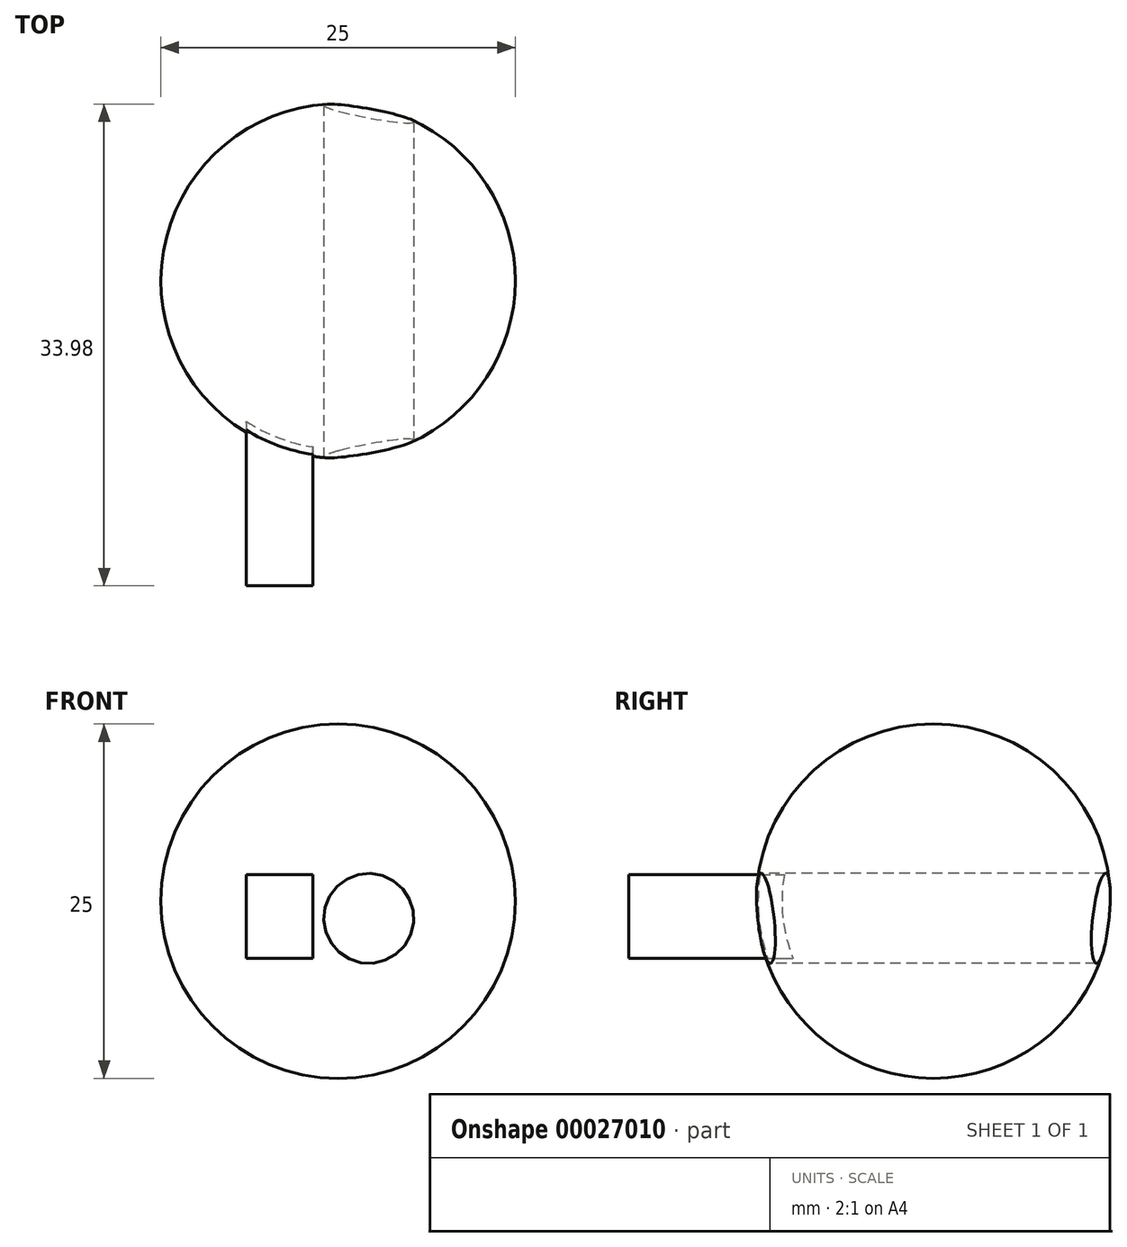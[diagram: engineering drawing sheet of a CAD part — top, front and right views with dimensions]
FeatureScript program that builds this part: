
annotation { "Feature Type Name" : "Feature", "Feature Type Description" : "" }
export const myFeature = defineFeature(function(context is Context, id is Id, definition is map)
    precondition{}
    {
        {
            var Q0;
            Q0=qCreatedBy(makeId("Front.planeOp"),FACE);
            var sketch = newSketch(context, id + "F0", { "sketchPlane" : qUnion([Q0])});
            skArc(sketch, "E0", {"start": v(-23.27, 31.46) * mm, "mid": v(-35.77, 18.96) * mm, "end": v(-23.27, 6.46) * mm});
            skLineSegment(sketch, "E1", {"start": v(-23.27, 31.46) * mm, "end": v(-23.27, 6.46) * mm});
            skSolve(sketch);
        }
        {
            var Q0;
            Q0=makeQuery(id+"F0.imprint","IMPRINT",FACE,{"disambiguationData":[TD([[makeQuery(id+"F0.imprint","IMPRINT",EDGE,{"derivedFrom":sQuery(id+"F0.wireOp",EDGE,"E0")}),1.0]])]});
            var Q1;
            Q1=sQuery(id+"F0.wireOp",EDGE,"E1");
            revolve(context, id + "F1", {"entities" : qUnion([Q0]), "axis" : qUnion([Q1]), "revolveType" : RevolveType.FULL});
        }
        {
            var Q0;
            Q0=qCreatedBy(makeId("Front.planeOp"),FACE);
            cPlane(context, id + "F2", {"entities" : qUnion([Q0]), "cplaneType" : CPlaneType.OFFSET, "offset" : 12.5 * mm, "width" : 152.4 * mm, "height" : 152.4 * mm});
        }
        {
            var Q0;
            Q0=qCreatedBy(id+"F2.planeOp",FACE);
            var sketch = newSketch(context, id + "F3", { "sketchPlane" : qUnion([Q0])});
            skCircle(sketch, "E2", {"center": v(-21.1, 17.75) * mm, "radius": 5 * mm});
            skSolve(sketch);
        }
        {
            var Q0;
            Q0=sQuery(id+"F3.wireOp",VERTEX,"E2.center");
            var Q1;
            Q1=makeQuery(id+"F1.opRevolve","SWEPT_BODY",BODY,{"disambiguationData":[OSD([sQuery(id+"F0.wireOp",EDGE,"E0"),sQuery(id+"F0.wireOp",EDGE,"E1")])]});
            hole(context, id + "F4", {"style" : HoleStyle.SIMPLE, "holeDiameter" : 6.35 * mm, "endStyle" : HoleEndStyle.THROUGH, "locations" : qUnion([Q0]), "scope" : qUnion([Q1])});
        }
        {
            var Q0;
            Q0=qCreatedBy(id+"F2.planeOp",FACE);
            var sketch = newSketch(context, id + "F5", { "sketchPlane" : qUnion([Q0])});
            skLineSegment(sketch, "E3.bottom", {"start": v(-25.06, 14.94) * mm, "end": v(-29.76, 14.94) * mm});
            skLineSegment(sketch, "E3.top", {"start": v(-25.06, 20.83) * mm, "end": v(-29.76, 20.83) * mm});
            skLineSegment(sketch, "E3.left", {"start": v(-25.06, 14.94) * mm, "end": v(-25.06, 20.83) * mm});
            skLineSegment(sketch, "E3.right", {"start": v(-29.76, 14.94) * mm, "end": v(-29.76, 20.83) * mm});
            skSolve(sketch);
        }
        {
            var Q0;
            Q0=makeQuery(id+"F5.imprint","IMPRINT",FACE,{"disambiguationData":[TD([[makeQuery(id+"F5.imprint","IMPRINT",EDGE,{"derivedFrom":sQuery(id+"F5.wireOp",EDGE,"E3.bottom")}),-1.0]])]});
            extrude(context, id + "F6", {"entities" : qUnion([Q0]), "operationType" : NewBodyOperationType.ADD, "depth" : 9 * mm, "hasSecondDirection" : true, "secondDirectionBound" : SecondDirectionBoundingType.UP_TO_NEXT, "secondDirectionOppositeDirection" : true, "secondDirectionDepth" : 25.4 * mm});
        }
    });
